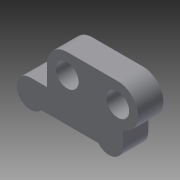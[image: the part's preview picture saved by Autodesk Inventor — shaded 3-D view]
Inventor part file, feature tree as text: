
AUTODESK INVENTOR PART (.ipt)
format: ipt  version: 2015 (Build 190159000, 159)  size: 106,496 bytes
history: native  units: mm
features: sketch x2, extrude x1, hole x1
ambient origin geometry x8: Origin, YZ Plane, XZ Plane, XY Plane, X Axis, Y Axis, Z Axis, Center Point
bodies: Solid1 (feature_tree)
feature tree (4):
  extrude  "Extrusion1"  Depth=16.0mm
  hole  "Hole1"  [1 undecoded]
  sketch  "Sketch1"  dims[d0=16.0mm d1=11.0mm]
  sketch  "Sketch3"  dims[d3=9.0mm d4=20.0mm d6=2.0mm d7=31.0mm d8=10.0mm d9=0.0mm d12=20.0mm d13=9.0mm d14=6.0mm d15=4.0mm d16=2.0mm d17=90.0deg d18=8.0mm d19=20.594885mm]
note: 1 required parameter value undecoded (feature->parameter linkage not recoverable at this tier; creation-order binding heuristic only, values carry confidence <= 0.55)
